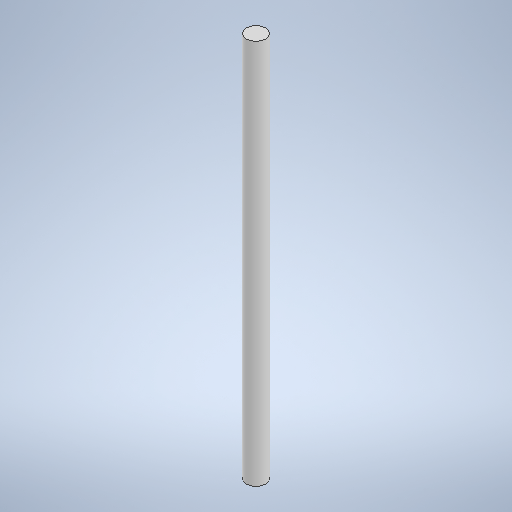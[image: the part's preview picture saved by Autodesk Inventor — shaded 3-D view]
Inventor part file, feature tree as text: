
AUTODESK INVENTOR PART (.ipt)
format: ipt  version: 2025.2 (Build 292293000, 293)  size: 233,472 bytes
history: native  units: mm
features: extrude x1, sketch x1
ambient origin geometry x8: Origin, YZ Plane, XZ Plane, XY Plane, X Axis, Y Axis, Z Axis, Center Point
bodies: Solid1 (feature_tree)
feature tree (2):
  extrude  "Extrusion1"  Depth=100.0mm TaperAngle=0.0deg
  sketch  "Sketch1"  dims[d0=5.0mm d1=100.0mm d2=0.0mm]
